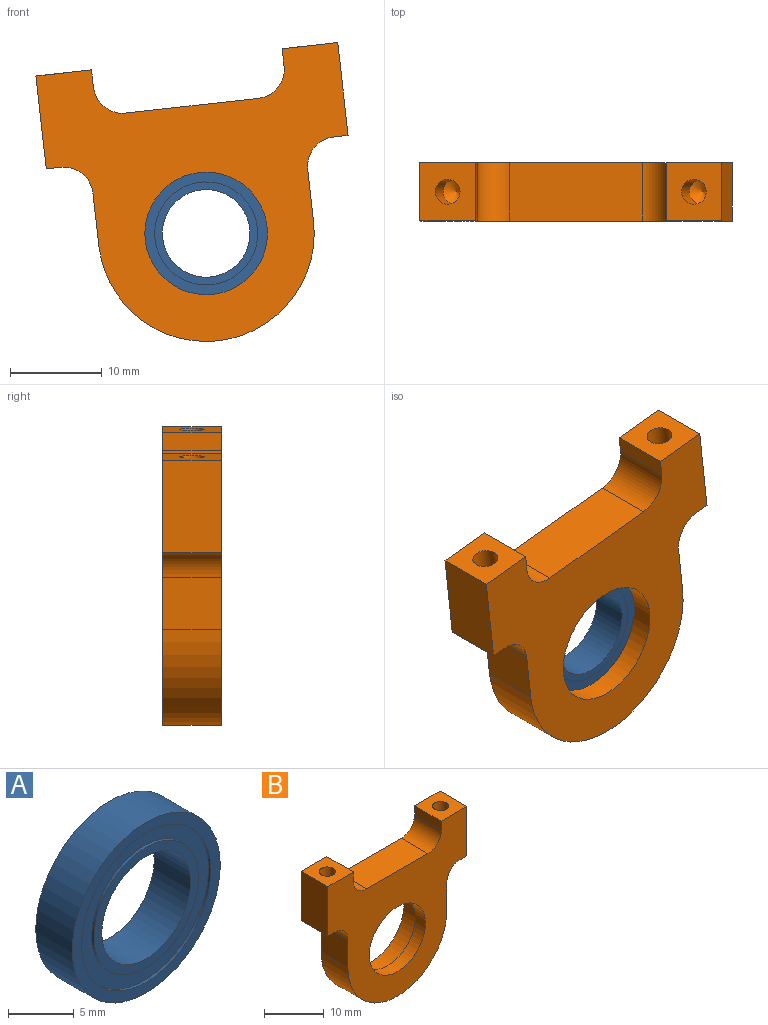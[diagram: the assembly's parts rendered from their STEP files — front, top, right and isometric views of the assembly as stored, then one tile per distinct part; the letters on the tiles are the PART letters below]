
ASSEMBLY  parts=2 mates=1
PART A: 12 faces, bbox 15.9x3.9x15.9 mm
  f0: cylinder r=5.6mm len=11.2mm, axis (0,-1,0), area 8.9mm2, adj f6,f11
  f1: cylinder r=6.93mm len=13.87mm, axis (0,-1,0), area 11.1mm2, adj f9,f11
  f2: cylinder r=5.6mm len=11.2mm, axis (0,1,0), area 8.9mm2, adj f7,f10
  f3: cylinder r=6.93mm len=13.87mm, axis (0,1,0), area 11.1mm2, adj f8,f10
  f4: cylinder r=4.76mm len=9.53mm, axis (0,-1,0), area 117mm2, adj f6,f7
  f5: cylinder r=7.94mm len=15.88mm, axis (0,-1,0), area 195.1mm2, adj f8,f9
  f6: plane 11.2x11.2mm, normal (0,-1,0), area 27.3mm2, adj f0,f4
  f7: plane 11.2x11.2mm, normal (0,1,0), area 27.3mm2, adj f2,f4
  f8: plane 15.88x15.88mm, normal (0,1,0), area 46.9mm2, adj f3,f5
  f9: plane 15.88x15.88mm, normal (0,-1,0), area 46.9mm2, adj f1,f5
  f10: plane 13.87x13.87mm, normal (0,1,0), area 52.5mm2, adj f2,f3
  f11: plane 13.87x13.87mm, normal (0,-1,0), area 52.5mm2, adj f0,f1
PART B: 25 faces, bbox 33x6.4x30.8 mm
  f0: cylinder r=6.67mm len=13.34mm, axis (0,1,0), area 100mm2, adj f19,f24
  f1: cylinder r=7.94mm len=15.88mm, axis (0,1,0), area 197.6mm2, adj f18,f24
  f2: cylinder r=1.35mm len=7.62mm, axis (0,0,1), area 64.8mm2, adj f3,f10
  f3: cone r=1.35mm half-angle=59deg, axis (0,0,1), area 6.7mm2, adj f2
  f4: cylinder r=1.35mm len=7.62mm, axis (0,0,1), area 64.8mm2, adj f5,f14
  f5: cone r=1.35mm half-angle=59deg, axis (0,0,1), area 6.7mm2, adj f4
  f6: cylinder r=11.75mm len=23.5mm, axis (0,-1,0), area 234.4mm2, adj f7,f17,f18,f19
  f7: plane 6.35x5.72mm, normal (-1,0,0), area 36.3mm2, adj f6,f18,f19,f20
  f8: plane 6.35x1.59mm, normal (0,0,-1), area 10.1mm2, adj f9,f18,f19,f20
  f9: plane 10.16x6.35mm, normal (-1,0,0), area 64.5mm2, adj f8,f10,f18,f19
  f10: plane 6.35x6.08mm, normal (0,0,1), area 32.9mm2, adj f2,f9,f11,f18,f19
  f11: plane 6.35x1.91mm, normal (1,0,0), area 12.1mm2, adj f10,f18,f19,f23
  f12: plane 14.51x6.35mm, normal (0,0,1), area 92.1mm2, adj f18,f19,f22,f23
  f13: plane 6.35x1.91mm, normal (-1,0,0), area 12.1mm2, adj f14,f18,f19,f22
  f14: plane 6.35x6.08mm, normal (0,0,1), area 32.9mm2, adj f4,f13,f15,f18,f19
  f15: plane 10.16x6.35mm, normal (1,0,0), area 64.5mm2, adj f14,f16,f18,f19
  f16: plane 6.35x1.59mm, normal (0,0,-1), area 10.1mm2, adj f15,f18,f19,f21
  f17: plane 6.35x5.72mm, normal (1,0,0), area 36.3mm2, adj f6,f18,f19,f21
  f18: plane 33.02x30.8mm, normal (0,1,0), area 465.9mm2, adj f1,f6,f7,f8,f9,f10,f11,f12
  f19: plane 33.02x30.8mm, normal (0,-1,0), area 524.2mm2, adj f0,f6,f7,f8,f9,f10,f11,f12
  f20: cylinder r=3.17mm len=6.35mm, axis (0,1,0), area 31.7mm2, adj f7,f8,f18,f19
  f21: cylinder r=3.17mm len=6.35mm, axis (0,1,0), area 31.7mm2, adj f16,f17,f18,f19
  f22: cylinder r=3.17mm len=6.35mm, axis (0,1,0), area 31.7mm2, adj f12,f13,f18,f19
  f23: cylinder r=3.17mm len=6.35mm, axis (0,1,0), area 31.7mm2, adj f11,f12,f18,f19
  f24: plane 15.88x15.88mm, normal (0,1,0), area 58.3mm2, adj f0,f1
PLACE A rot(axis=(0,-1,0),6.3deg) t=(8.56,15.39,24.4)mm
PLACE B rot(axis=(0,-1,0),6.3deg) t=(8.56,13,24.4)mm
MATE fastened B.f0 <-> A.f0  axis (0,1,0) through (8.56,13,24.4)mm
